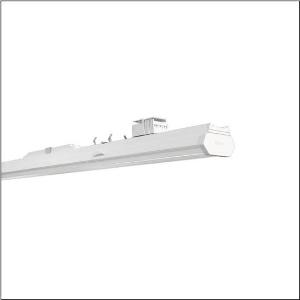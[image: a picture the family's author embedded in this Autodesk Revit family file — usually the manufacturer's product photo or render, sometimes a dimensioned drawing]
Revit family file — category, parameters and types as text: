
# Revit family: licross_r__11_protected_ho_51tp12dn4fxm3s_598f
name_source: partatom
category: Lighting Fixtures
units: mm (PartAtom-declared; Revit-internal decimal feet)

## family parameters
Cut with Voids When Loaded = No
Host = Face
Light Source = No
Part Type = Normal
Room Calculation Point = No
Round Connector Dimension = Use Diameter
Shared = No

## types (1)
- --- (1 x LED, 970 lm, 7.4 W, 4000K)
    Apparent Load = 7 VA
    CIE Flux Codes = 70 91 97 98 100
    Color Rendering = 80
    Color Temperature = 4000K
    Default Elevation = 1800 mm
    Description = Licross® 11 Protected HO, luminaire insert, of sheet steel, galvanised, coil coated, white, length: 1.500mm, width: 90mm, height: 101mm, LED rated luminous flux: 15.270lm, light colour: 840, control gear: DALI 2 (for two DALI lines), with plug, 6-pole, with phase selection, for trunking rail, 14-core, mains connection: 220..240V, AC, 50/60Hz, rated input power: 91W, for trunking rail, 14-core, halogen-free wiring, for emergency light function, converter,control gear: single battery element, battery: LiFePO4, 9Ah, primary light control with lens, of plastic, primary optical cover: cover, of PMMA, light emission: direct distribution, primary light characteristic: symmetric, protection rating (complete): IP64, insulation class (complete): insulation class I (protective earthing), certification: CE, UKCA, protection symbol: D if used in an environment with conductive dust loads with corresponding accessories, impact resistance: IK06, permissible ambient temperature for indoor applications: +5..+30°C, standard: EN 60598-2-22, LABS conformity tested according to VDMA 24364:2018-05, reducing of maximum allowable ambient temperature of 5°C with ceiling mounting, corresponds to IFS (International Featured Standards) requirements for safety and quality in the food industry, packaging unit: 1 piece
    Height = 92 mm
    Lamp = 1 x LED
    Lamp Light Flux = 970 lm
    Lamp Power = 7.4 W
    Lamp count = 1
    Length = 1500 mm
    Luminous efficacy = 131 lm/W
    Manufacturer = Siteco
    ModVariant = No
    Model = 51TP12DN4FXM3S
    Mounting Place = Ceiling
    Mounting Type = Pendant
    Number of Poles = 1
    OnlyDefault = Yes
    Power Factor = 1
    Product Name = Licross® 11 Protected HO
    Product group = luminaire insert
    ProductGroupID = 901
    Protection Class = Protection class I
    Protection Degree = IP 64
    RLX_Detail_Level = 1
    RLX_Emergency_Light_Flux = 0 lm
    RLX_Emergency_Type = 0
    RLX_Emergency_Type_DB = No
    RlxData = <blob elided: 24977 chars, md5=ca561ae4>
    Socket = socket
    Standby Power = 0 W
    System Light Flux = 970 lm
    System Power = 7 W
    Type Comments = : emergency light operation: 3 h
    Type Image = l_1256148.jpg
    URL = http://relux.com
    VarID = @adj_059795
    Voltage = 0 V
    Weight = 0.00 kg
    Width = 88 mm

## geometry (parser evidence)
native form markers: Blend x4, Sweep x11
no freeform markers — native parametric forms only
